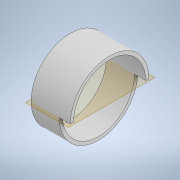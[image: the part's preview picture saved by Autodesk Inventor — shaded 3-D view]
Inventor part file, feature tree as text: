
AUTODESK INVENTOR PART (.ipt)
format: ipt  version: 2021 (Build 250183000, 183)  size: 115,200 bytes
history: native  units: in
note: dims shown in document units (in); Inventor stores cm internally (conversion verified against a paired STEP export)
features: extrude x2, sketch x2
ambient origin geometry x8: Origin, YZ Plane, XZ Plane, XY Plane, X Axis, Y Axis, Z Axis, Center Point
bodies: Solid1 (feature_tree)
feature tree (4):
  extrude  "Extrusion1"  Depth=6.0in
  extrude  "Extrusion2"  Depth=0.85in
  sketch  "Sketch1"  dims[d0=5.5in d1=6.0in]
  sketch  "Sketch2"  dims[d2=3.0in d3=0.0in d4=0.85in d5=3.0in d6=0.0in]
